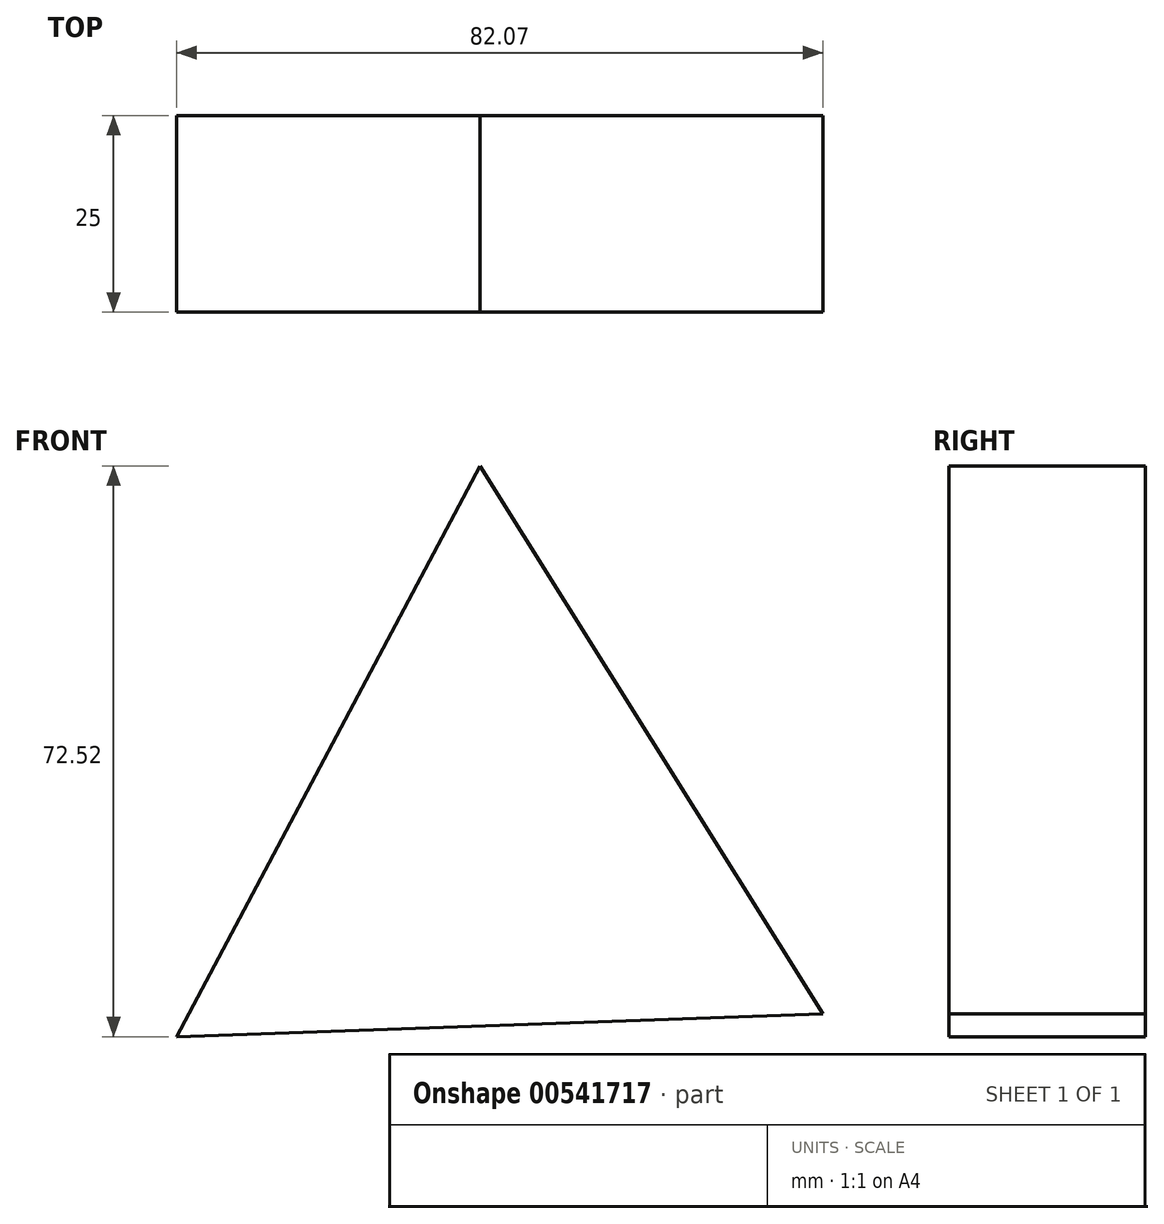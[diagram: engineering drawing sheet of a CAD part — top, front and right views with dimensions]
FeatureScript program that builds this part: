
annotation { "Feature Type Name" : "Feature", "Feature Type Description" : "" }
export const myFeature = defineFeature(function(context is Context, id is Id, definition is map)
    precondition{}
    {
        {
            var Q0;
            Q0=qCreatedBy(makeId("Front.planeOp"),FACE);
            var sketch = newSketch(context, id + "F0", { "sketchPlane" : qUnion([Q0])});
            skLineSegment(sketch, "E0", {"start": v(0, 38.8) * mm, "end": v(-38.53, -33.7) * mm});
            skLineSegment(sketch, "E1", {"start": v(-38.53, -33.7) * mm, "end": v(43.54, -30.81) * mm});
            skLineSegment(sketch, "E2", {"start": v(43.54, -30.81) * mm, "end": v(0, 38.8) * mm});
            skSolve(sketch);
        }
        {
            var Q0;
            Q0 = qSketchRegion(id + "F0", true);
            extrude(context, id + "F1", {"entities" : qUnion([Q0]), "depth" : 25 * mm, "offsetDistance" : 25 * mm});
        }
    });
